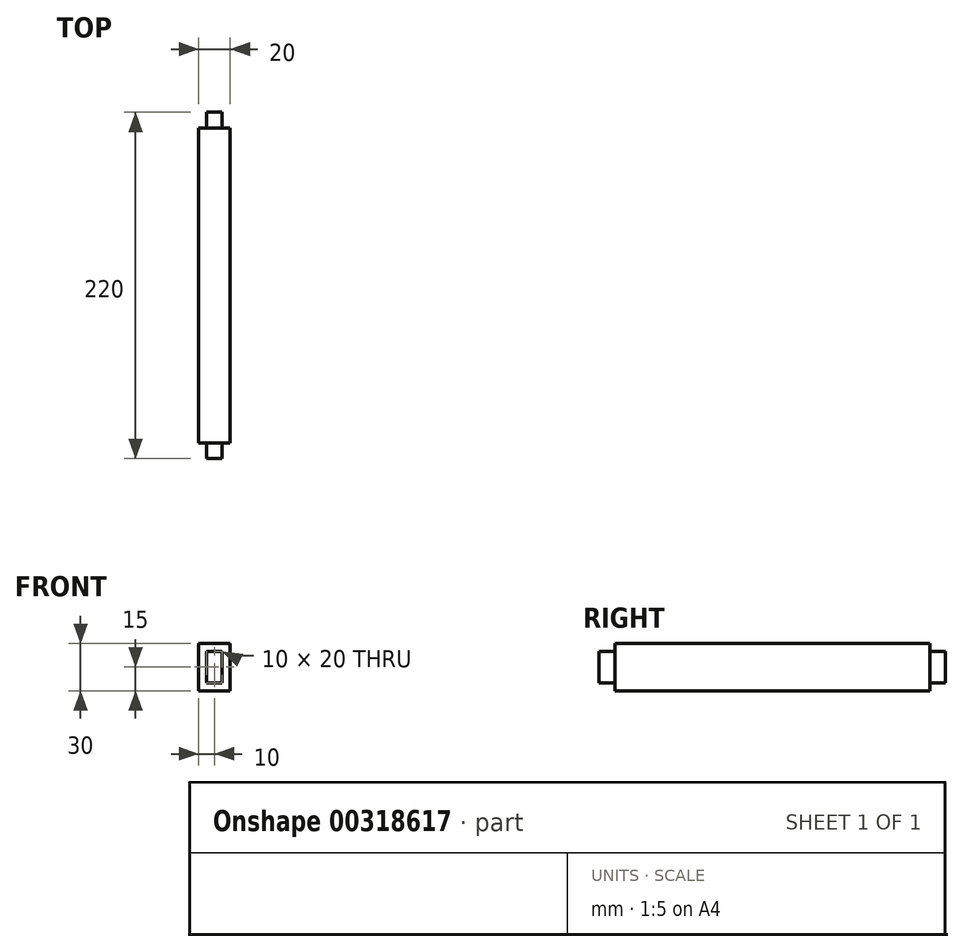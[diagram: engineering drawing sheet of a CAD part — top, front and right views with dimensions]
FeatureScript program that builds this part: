
annotation { "Feature Type Name" : "Feature", "Feature Type Description" : "" }
export const myFeature = defineFeature(function(context is Context, id is Id, definition is map)
    precondition{}
    {
        {
            var Q0;
            Q0=qCreatedBy(makeId("Front.planeOp"),FACE);
            var sketch = newSketch(context, id + "F0", { "sketchPlane" : qUnion([Q0])});
            skLineSegment(sketch, "E0.rect.bottom", {"start": v(10, -15) * mm, "end": v(-10, -15) * mm});
            skLineSegment(sketch, "E0.rect.top", {"start": v(10, 15) * mm, "end": v(-10, 15) * mm});
            skLineSegment(sketch, "E0.rect.left", {"start": v(10, -15) * mm, "end": v(10, 15) * mm});
            skLineSegment(sketch, "E0.rect.right", {"start": v(-10, -15) * mm, "end": v(-10, 15) * mm});
            skPoint(sketch, "E0.rect.middle", {"position": v(0, 0) * mm});
            skSolve(sketch);
        }
        {
            var Q0;
            Q0=qSketchRegion(id+"F0",true);
            extrude(context, id + "F1", {"entities" : qUnion([Q0]), "depth" : 100 * mm});
        }
        {
            var Q0;
            Q0=makeQuery(id+"F1.opExtrude","CAP_FACE",FACE,{"disambiguationData":[OSD([sQuery(id+"F0.wireOp",EDGE,"E0.rect.bottom"),sQuery(id+"F0.wireOp",EDGE,"E0.rect.top"),sQuery(id+"F0.wireOp",EDGE,"E0.rect.left"),sQuery(id+"F0.wireOp",EDGE,"E0.rect.right")])],"isStart":false});
            var sketch = newSketch(context, id + "F2", { "sketchPlane" : qUnion([Q0])});
            skLineSegment(sketch, "E1.rect.bottom", {"start": v(5, -10) * mm, "end": v(-5, -10) * mm});
            skLineSegment(sketch, "E1.rect.top", {"start": v(5, 10) * mm, "end": v(-5, 10) * mm});
            skLineSegment(sketch, "E1.rect.left", {"start": v(5, -10) * mm, "end": v(5, 10) * mm});
            skLineSegment(sketch, "E1.rect.right", {"start": v(-5, -10) * mm, "end": v(-5, 10) * mm});
            skPoint(sketch, "E1.rect.middle", {"position": v(0, 0) * mm});
            skSolve(sketch);
        }
        {
            var Q0;
            Q0=qSketchRegion(id+"F2",true);
            extrude(context, id + "F3", {"entities" : qUnion([Q0]), "operationType" : NewBodyOperationType.ADD, "depth" : 10 * mm});
        }
        {
            var Q0;
            Q0=makeQuery(id+"F1.opExtrude","SWEPT_BODY",BODY,{"disambiguationData":[OSD([sQuery(id+"F0.wireOp",EDGE,"E0.rect.bottom"),sQuery(id+"F0.wireOp",EDGE,"E0.rect.top"),sQuery(id+"F0.wireOp",EDGE,"E0.rect.left"),sQuery(id+"F0.wireOp",EDGE,"E0.rect.right")])]});
            var Q1;
            Q1=qCreatedBy(makeId("Front.planeOp"),FACE);
            mirror(context, id + "F4", {"operationType" : NewBodyOperationType.ADD, "entities" : qUnion([Q0]), "mirrorPlane" : qUnion([Q1])});
        }
    });
